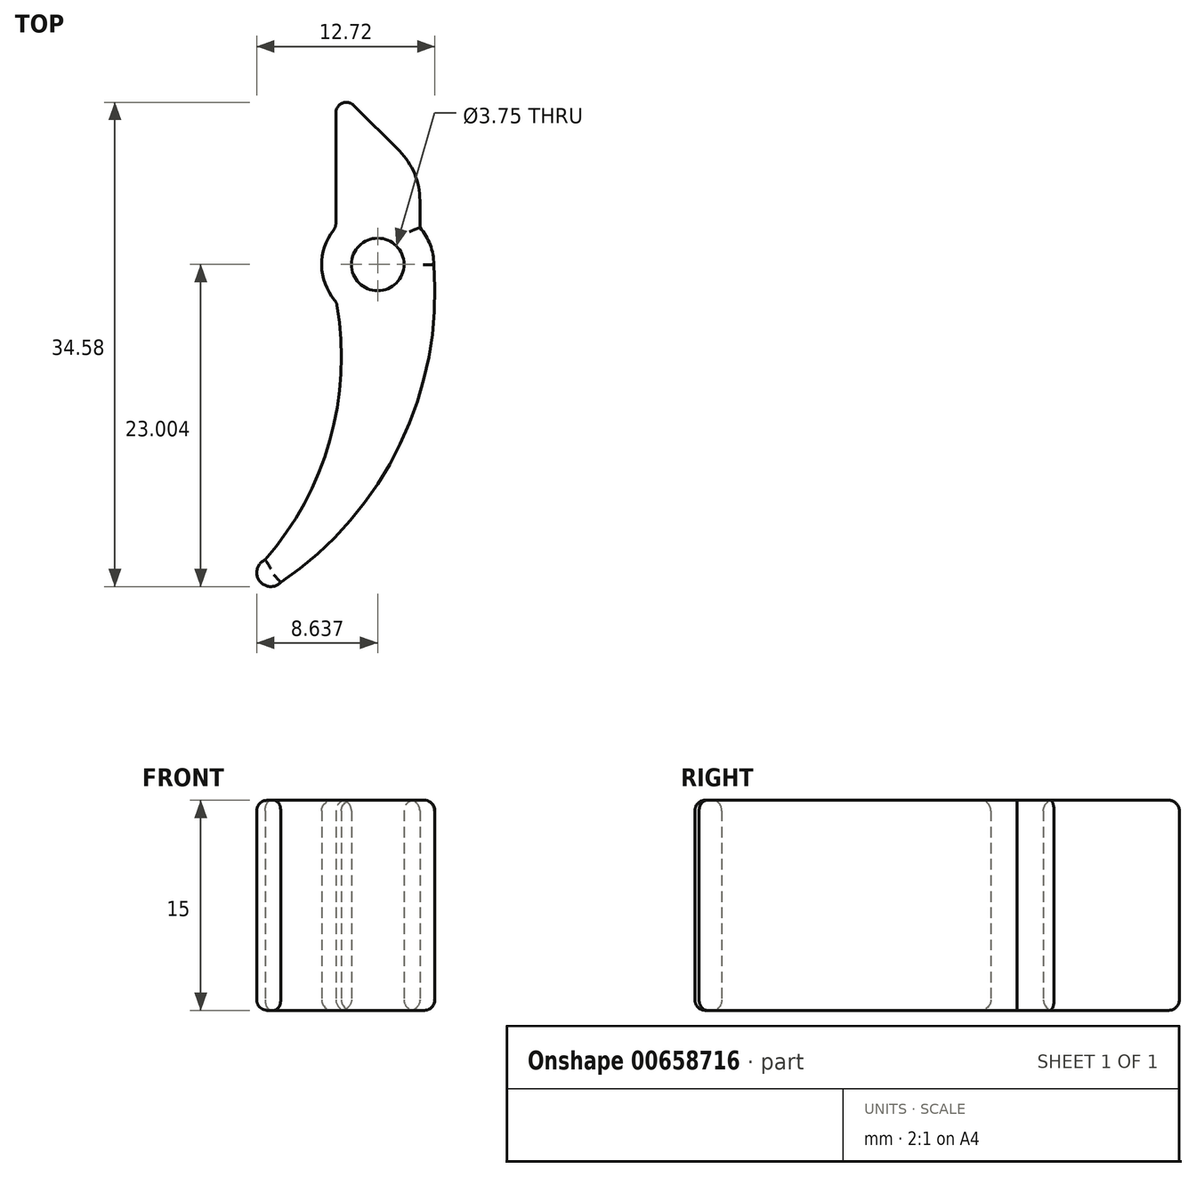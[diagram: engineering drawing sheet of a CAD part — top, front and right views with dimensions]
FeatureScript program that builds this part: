
annotation { "Feature Type Name" : "Feature", "Feature Type Description" : "" }
export const myFeature = defineFeature(function(context is Context, id is Id, definition is map)
    precondition{}
    {
        {
            var Q0;
            Q0=qCreatedBy(makeId("Top.planeOp"),FACE);
            var sketch = newSketch(context, id + "F0", { "sketchPlane" : qUnion([Q0])});
            skCircle(sketch, "E0", {"center": v(0.69, 0.08) * mm, "radius": 4 * mm});
            skCircle(sketch, "E1", {"center": v(0.69, 0.08) * mm, "radius": 1.88 * mm});
            skArc(sketch, "E2", {"start": v(-7.35, -21) * mm, "mid": v(-2.7, -12.4) * mm, "end": v(-2.26, -2.62) * mm});
            skArc(sketch, "E3", {"start": v(-7.35, -21) * mm, "mid": v(-7.77, -22.48) * mm, "end": v(-6.24, -22.62) * mm});
            skArc(sketch, "E4", {"start": v(-6.24, -22.62) * mm, "mid": v(2.3, -12.74) * mm, "end": v(4.69, 0.08) * mm});
            skLineSegment(sketch, "E5.bottom", {"start": v(-2.3, 6.72) * mm, "end": v(3.7, 6.72) * mm});
            skLineSegment(sketch, "E5.left", {"start": v(-2.3, 6.72) * mm, "end": v(-2.3, 2.74) * mm});
            skLineSegment(sketch, "E5.right", {"start": v(3.7, 6.72) * mm, "end": v(3.7, 2.72) * mm});
            skPoint(sketch, "E5.middle", {"position": v(0.69, 3.08) * mm});
            skLineSegment(sketch, "E6", {"start": v(-2.3, 6.72) * mm, "end": v(-2.3, 12.72) * mm});
            skLineSegment(sketch, "E7", {"start": v(-2.3, 12.72) * mm, "end": v(3.7, 6.72) * mm});
            skSolve(sketch);
        }
        {
            var Q0;
            Q0=makeQuery(id+"F0.imprint","IMPRINT",FACE,{"disambiguationData":[TD([[makeQuery(id+"F0.imprint","IMPRINT",EDGE,{"derivedFrom":sQuery(id+"F0.wireOp",EDGE,"E5.bottom")}),1.0]])]});
            var Q1;
            Q1=makeQuery(id+"F0.imprint","IMPRINT",FACE,{"disambiguationData":[TD([[makeQuery(id+"F0.imprint","IMPRINT",EDGE,{"derivedFrom":sQuery(id+"F0.wireOp",EDGE,"E5.bottom")}),-1.0]])]});
            var Q2;
            Q2=makeQuery(id+"F0.imprint","IMPRINT",FACE,{"disambiguationData":[TD([[makeQuery(id+"F0.imprint","IMPRINT",EDGE,{"derivedFrom":sQuery(id+"F0.wireOp",EDGE,"E1")}),-1.0]])]});
            var Q3;
            {var subQ0=sQuery(id+"F0.wireOp",EDGE,"E2");Q3=makeQuery(id+"F0.imprint","IMPRINT",FACE,{"disambiguationData":[TD([[makeQuery(id+"F0.imprint","IMPRINT",EDGE,{"derivedFrom":subQ0}),-1.0]])]});}
            extrude(context, id + "F1", {"entities" : qUnion([Q0, Q1, Q2, Q3]), "depth" : 15 * mm, "offsetDistance" : 25 * mm});
        }
        {
            var Q0;
            Q0=makeQuery(id+"F1.opExtrude","CAP_FACE",FACE,{"disambiguationData":[OSD([sQuery(id+"F0.wireOp",EDGE,"E0"),sQuery(id+"F0.wireOp",EDGE,"E1"),sQuery(id+"F0.wireOp",EDGE,"E2"),sQuery(id+"F0.wireOp",EDGE,"E3"),sQuery(id+"F0.wireOp",EDGE,"E4"),sQuery(id+"F0.wireOp",EDGE,"E5.left"),sQuery(id+"F0.wireOp",EDGE,"E5.right"),sQuery(id+"F0.wireOp",EDGE,"E6"),sQuery(id+"F0.wireOp",EDGE,"E7")])],"isStart":false});
            var Q1;
            Q1=makeQuery(id+"F1.opExtrude","CAP_FACE",FACE,{"disambiguationData":[OSD([sQuery(id+"F0.wireOp",EDGE,"E0"),sQuery(id+"F0.wireOp",EDGE,"E1"),sQuery(id+"F0.wireOp",EDGE,"E2"),sQuery(id+"F0.wireOp",EDGE,"E3"),sQuery(id+"F0.wireOp",EDGE,"E4"),sQuery(id+"F0.wireOp",EDGE,"E5.left"),sQuery(id+"F0.wireOp",EDGE,"E5.right"),sQuery(id+"F0.wireOp",EDGE,"E6"),sQuery(id+"F0.wireOp",EDGE,"E7")])],"isStart":true});
            var Q2;
            {var subQ0=sQuery(id+"F0.wireOp",EDGE,"E0");Q2=makeQuery(id+"F1.opExtrude","SWEPT_FACE",FACE,{"disambiguationData":[OSD([subQ0]),TDD([makeQuery(id+"F0.imprint","IMPRINT",EDGE,{"disambiguationData":[TD([[makeQuery(id+"F0.imprint","INTERSECT",VERTEX,{"derivedFrom":[subQ0,sQuery(id+"F0.wireOp",EDGE,"E2")]}),1.0]])],"derivedFrom":subQ0})])]});}
            var Q3;
            Q3=makeQuery(id+"F1.opExtrude","SWEPT_FACE",FACE,{"disambiguationData":[OSD([sQuery(id+"F0.wireOp",EDGE,"E5.left"),sQuery(id+"F0.wireOp",EDGE,"E6")])]});
            fillet(context, id + "F2", {"entities" : qUnion([Q0, Q1, Q2, Q3]), "radius" : .75 * mm, "tangentPropagation" : true, "allowEdgeOverflow" : false});
        }
        {
            var Q0;
            Q0=makeQuery(id+"F1.opExtrude","SWEPT_EDGE",EDGE,{"disambiguationData":[OSD([sQuery(id+"F0.wireOp",EDGE,"E5.bottom"),sQuery(id+"F0.wireOp",EDGE,"E5.right"),sQuery(id+"F0.wireOp",EDGE,"E7")])]});
            var Q1;
            {var subQ0=sQuery(id+"F0.wireOp",EDGE,"E2");var subQ1=sQuery(id+"F0.wireOp",EDGE,"E0");Q1=makeQuery(id+"F2.opFillet","BLEND_EDGE",EDGE,{"blendedFrom":[makeQuery(id+"F1.opExtrude","SWEPT_EDGE",EDGE,{"disambiguationData":[OSD([subQ1,subQ0])]}),makeQuery(id+"F1.opExtrude","SWEPT_FACE",FACE,{"disambiguationData":[OSD([subQ1]),TDD([makeQuery(id+"F0.imprint","IMPRINT",EDGE,{"disambiguationData":[TD([[makeQuery(id+"F0.imprint","INTERSECT",VERTEX,{"derivedFrom":[subQ1,subQ0]}),1.0]])],"derivedFrom":subQ1})])]})],"blendedInto":[makeQuery(id+"F1.opExtrude","SWEPT_FACE",FACE,{"disambiguationData":[OSD([subQ1]),TDD([makeQuery(id+"F0.imprint","IMPRINT",EDGE,{"disambiguationData":[TD([[makeQuery(id+"F0.imprint","INTERSECT",VERTEX,{"derivedFrom":[subQ1,subQ0]}),1.0]])],"derivedFrom":subQ1})])]})]});}
            var Q2;
            {var subQ0=sQuery(id+"F0.wireOp",EDGE,"E2");Q2=makeQuery(id+"F2.opFillet","BLEND_EDGE",EDGE,{"blendedFrom":[makeQuery(id+"F1.opExtrude","SWEPT_EDGE",EDGE,{"disambiguationData":[OSD([sQuery(id+"F0.wireOp",EDGE,"E0"),subQ0])]}),makeQuery(id+"F1.opExtrude","SWEPT_FACE",FACE,{"disambiguationData":[OSD([subQ0])]})],"blendedInto":[makeQuery(id+"F1.opExtrude","SWEPT_FACE",FACE,{"disambiguationData":[OSD([subQ0])]})]});}
            fillet(context, id + "F3", {"entities" : qUnion([Q0, Q1, Q2]), "radius" : 5 * mm, "tangentPropagation" : true, "allowEdgeOverflow" : false});
        }
    });
